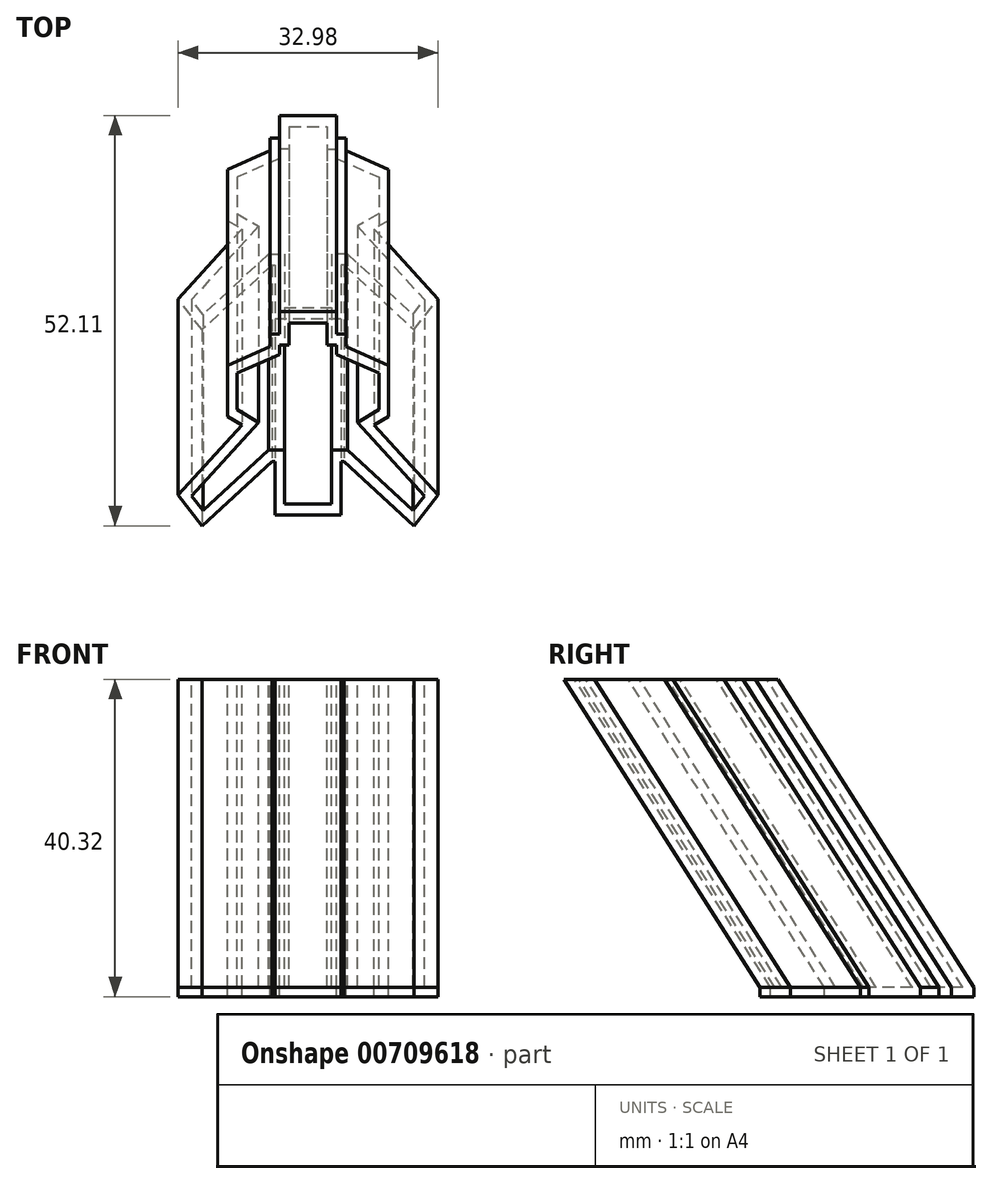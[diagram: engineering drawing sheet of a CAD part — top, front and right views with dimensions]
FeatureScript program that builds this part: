
annotation { "Feature Type Name" : "Feature", "Feature Type Description" : "" }
export const myFeature = defineFeature(function(context is Context, id is Id, definition is map)
    precondition{}
    {
        {
            var Q0;
            Q0=qCreatedBy(makeId("Top.planeOp"),FACE);
            var sketch = newSketch(context, id + "F0", { "sketchPlane" : qUnion([Q0])});
            skLineSegment(sketch, "E0", {"start": v(5, -3.24) * mm, "end": v(3, -3.24) * mm});
            skLineSegment(sketch, "E1", {"start": v(3, -3.24) * mm, "end": v(3, -9) * mm});
            skLineSegment(sketch, "E2", {"start": v(5, 0) * mm, "end": v(9, 2) * mm});
            skLineSegment(sketch, "E3", {"start": v(9, 5) * mm, "end": v(5, 7) * mm, "construction": true});
            skLineSegment(sketch, "E4", {"start": v(5, 7) * mm, "end": v(5, 9) * mm, "construction": true});
            skLineSegment(sketch, "E5", {"start": v(9, 5) * mm, "end": v(9, 2) * mm});
            skLineSegment(sketch, "E6.bottom", {"start": v(67.07, 3.45) * mm, "end": v(65.87, 3.45) * mm});
            skLineSegment(sketch, "E6.left", {"start": v(67.07, 3.45) * mm, "end": v(67.07, 4.65) * mm});
            skPoint(sketch, "E6.middle", {"position": v(53.07, 12.45) * mm});
            skLineSegment(sketch, "E7", {"start": v(67.07, 3.45) * mm, "end": v(67.07, 4.65) * mm, "construction": true});
            skLineSegment(sketch, "E8", {"start": v(58.07, 12.45) * mm, "end": v(67.07, 4.65) * mm});
            skLineSegment(sketch, "E9", {"start": v(67.07, 3.45) * mm, "end": v(65.87, 3.45) * mm, "construction": true});
            skLineSegment(sketch, "E10", {"start": v(65.87, 3.45) * mm, "end": v(58.07, 10.2) * mm});
            skLineSegment(sketch, "E11", {"start": v(58.07, 10.2) * mm, "end": v(58.07, 9.2) * mm});
            skLineSegment(sketch, "E12", {"start": v(58.07, 9.2) * mm, "end": v(56.07, 9.2) * mm});
            skLineSegment(sketch, "E13", {"start": v(56.07, 9.2) * mm, "end": v(56.07, 3.45) * mm});
            skLineSegment(sketch, "E14", {"start": v(56.07, 3.45) * mm, "end": v(53.07, 3.45) * mm});
            skLineSegment(sketch, "E15", {"start": v(58.07, 12.45) * mm, "end": v(62.07, 14.45) * mm});
            skLineSegment(sketch, "E16", {"start": v(62.07, 17.45) * mm, "end": v(58.07, 19.45) * mm});
            skLineSegment(sketch, "E17", {"start": v(58.07, 19.45) * mm, "end": v(58.07, 21.45) * mm});
            skLineSegment(sketch, "E18", {"start": v(62.07, 17.45) * mm, "end": v(62.07, 14.45) * mm});
            skLineSegment(sketch, "E19", {"start": v(58.07, 21.45) * mm, "end": v(53.07, 21.45) * mm});
            skLineSegment(sketch, "E20", {"start": v(3, -9) * mm, "end": v(0, -9) * mm});
            skLineSegment(sketch, "E21", {"start": v(5, 0) * mm, "end": v(6, 0) * mm});
            skLineSegment(sketch, "E22", {"start": v(0, 15.56) * mm, "end": v(0, -14.94) * mm, "construction": true});
            skPoint(sketch, "E23", {"position": v(14.8, -8.14) * mm});
            skPoint(sketch, "E24", {"position": v(13.33, -9.72) * mm});
            skLineSegment(sketch, "E25", {"start": v(5, -3.24) * mm, "end": v(13.33, -9.72) * mm});
            skLineSegment(sketch, "E26", {"start": v(6, 0) * mm, "end": v(14.8, -8.14) * mm});
            skLineSegment(sketch, "E27", {"start": v(13.33, -9.72) * mm, "end": v(14.8, -8.14) * mm});
            skLineSegment(sketch, "E28", {"start": v(0, 10.4) * mm, "end": v(2.4, 10.4) * mm});
            skLineSegment(sketch, "E29", {"start": v(2.4, 10.4) * mm, "end": v(2.4, 8) * mm});
            skLineSegment(sketch, "E30", {"start": v(2.4, 8) * mm, "end": v(3.6, 8) * mm});
            skLineSegment(sketch, "E31", {"start": v(3.6, 8) * mm, "end": v(3.6, 7) * mm});
            skLineSegment(sketch, "E32", {"start": v(3.6, 7) * mm, "end": v(9, 5) * mm});
            skLineSegment(sketch, "E33.MirrorCS", {"start": v(-13.33, -9.72) * mm, "end": v(-14.8, -8.14) * mm});
            skLineSegment(sketch, "E34.MirrorCS", {"start": v(-3.6, 8) * mm, "end": v(-3.6, 7) * mm});
            skLineSegment(sketch, "E35.MirrorCS", {"start": v(-2.4, 8) * mm, "end": v(-3.6, 8) * mm});
            skLineSegment(sketch, "E36.MirrorCS", {"start": v(-5, 0) * mm, "end": v(-6, 0) * mm});
            skLineSegment(sketch, "E37.MirrorCS", {"start": v(-5, -3.24) * mm, "end": v(-3, -3.24) * mm});
            skLineSegment(sketch, "E38.MirrorCS", {"start": v(-2.4, 10.4) * mm, "end": v(-2.4, 8) * mm});
            skLineSegment(sketch, "E39.MirrorCS", {"start": v(-3, -3.24) * mm, "end": v(-3, -9) * mm});
            skLineSegment(sketch, "E40.MirrorCS", {"start": v(-6, 0) * mm, "end": v(-14.8, -8.14) * mm});
            skLineSegment(sketch, "E41.MirrorCS", {"start": v(-3, -9) * mm, "end": v(0, -9) * mm});
            skLineSegment(sketch, "E42.MirrorCS", {"start": v(-3.6, 7) * mm, "end": v(-9, 5) * mm});
            skLineSegment(sketch, "E43.MirrorCS", {"start": v(-5, -3.24) * mm, "end": v(-13.33, -9.72) * mm});
            skLineSegment(sketch, "E44.MirrorCS", {"start": v(-9, 5) * mm, "end": v(-9, 2) * mm});
            skLineSegment(sketch, "E45.MirrorCS", {"start": v(-5, 0) * mm, "end": v(-9, 2) * mm});
            skLineSegment(sketch, "E46.MirrorCS", {"start": v(0, 10.4) * mm, "end": v(-2.4, 10.4) * mm});
            skPoint(sketch, "E47.MirrorP", {"position": v(-14.8, -8.14) * mm});
            skPoint(sketch, "E48.MirrorP", {"position": v(-13.33, -9.72) * mm});
            skLineSegment(sketch, "E49.0", {"start": v(-7.74, 0.03) * mm, "end": v(-16.5, -8.07) * mm});
            skLineSegment(sketch, "E49.1", {"start": v(-13.46, -11.35) * mm, "end": v(-16.5, -8.07) * mm});
            skLineSegment(sketch, "E49.2", {"start": v(-4.59, -4.44) * mm, "end": v(-13.46, -11.35) * mm});
            skLineSegment(sketch, "E49.3", {"start": v(4.8, 9.2) * mm, "end": v(4.8, 7.84) * mm});
            skLineSegment(sketch, "E49.4", {"start": v(3.6, 9.2) * mm, "end": v(4.8, 9.2) * mm});
            skLineSegment(sketch, "E49.5", {"start": v(3.6, 11.6) * mm, "end": v(3.6, 9.2) * mm});
            skLineSegment(sketch, "E49.6", {"start": v(0, 11.6) * mm, "end": v(3.6, 11.6) * mm});
            skLineSegment(sketch, "E49.7", {"start": v(0, 11.6) * mm, "end": v(-3.6, 11.6) * mm});
            skLineSegment(sketch, "E49.8", {"start": v(-3.6, 11.6) * mm, "end": v(-3.6, 9.2) * mm});
            skLineSegment(sketch, "E49.9", {"start": v(-10.2, 5.84) * mm, "end": v(-10.2, 1.26) * mm});
            skLineSegment(sketch, "E49.10", {"start": v(-4.8, 7.84) * mm, "end": v(-10.2, 5.84) * mm});
            skLineSegment(sketch, "E49.11", {"start": v(-4.8, 9.2) * mm, "end": v(-4.8, 7.84) * mm});
            skLineSegment(sketch, "E49.12", {"start": v(-3.6, 9.2) * mm, "end": v(-4.8, 9.2) * mm});
            skLineSegment(sketch, "E49.13", {"start": v(4.8, 7.84) * mm, "end": v(10.2, 5.84) * mm});
            skLineSegment(sketch, "E49.14", {"start": v(10.2, 5.84) * mm, "end": v(10.2, 1.26) * mm});
            skLineSegment(sketch, "E49.15", {"start": v(7.74, 0.03) * mm, "end": v(10.2, 1.26) * mm});
            skLineSegment(sketch, "E49.16", {"start": v(-7.74, 0.03) * mm, "end": v(-10.2, 1.26) * mm});
            skLineSegment(sketch, "E49.17", {"start": v(7.74, 0.03) * mm, "end": v(16.5, -8.07) * mm});
            skLineSegment(sketch, "E49.18", {"start": v(13.46, -11.35) * mm, "end": v(16.5, -8.07) * mm});
            skLineSegment(sketch, "E49.19", {"start": v(4.59, -4.44) * mm, "end": v(13.46, -11.35) * mm});
            skLineSegment(sketch, "E49.20", {"start": v(4.59, -4.44) * mm, "end": v(4.2, -4.44) * mm});
            skLineSegment(sketch, "E49.21", {"start": v(4.2, -4.44) * mm, "end": v(4.2, -10.2) * mm});
            skLineSegment(sketch, "E49.22", {"start": v(4.2, -10.2) * mm, "end": v(0, -10.2) * mm});
            skLineSegment(sketch, "E49.23", {"start": v(-4.2, -10.2) * mm, "end": v(0, -10.2) * mm});
            skLineSegment(sketch, "E49.24", {"start": v(-4.2, -4.44) * mm, "end": v(-4.2, -10.2) * mm});
            skLineSegment(sketch, "E49.25", {"start": v(-4.59, -4.44) * mm, "end": v(-4.2, -4.44) * mm});
            skSolve(sketch);
        }
        {
            var Q0;
            Q0=makeQuery(id+"F0.imprint","IMPRINT",FACE,{"disambiguationData":[TD([[makeQuery(id+"F0.imprint","IMPRINT",EDGE,{"derivedFrom":sQuery(id+"F0.wireOp",EDGE,"E0")}),1.0]])]});
            extrude(context, id + "F1", {"entities" : qUnion([Q0]), "depth" : 3 * mm, "offsetDistance" : 25 * mm});
        }
        {
            var Q0;
            Q0=qCreatedBy(makeId("Top.planeOp"),FACE);
            var sketch = newSketch(context, id + "F2", { "sketchPlane" : qUnion([Q0])});
            skLineSegment(sketch, "E50", {"start": v(-27.03, 0) * mm, "end": v(31.48, 0) * mm});
            skSolve(sketch);
        }
        {
            var Q0;
            Q0=sQuery(id+"F2.wireOp",EDGE,"E50");
            cPlane(context, id + "F3", {"entities" : qUnion([Q0]), "cplaneType" : CPlaneType.LINE_ANGLE, "offset" : 25 * mm, "angle" : 57.5 * degree, "oppositeDirection" : true, "width" : 150 * mm, "height" : 150 * mm});
        }
        {
            var Q0;
            Q0=qCreatedBy(id+"F3.planeOp",FACE);
            var sketch = newSketch(context, id + "F4", { "sketchPlane" : qUnion([Q0])});
            skLineSegment(sketch, "E51", {"start": v(-5, 3.55) * mm, "end": v(-3, 3.55) * mm});
            skLineSegment(sketch, "E52", {"start": v(-3, 3.55) * mm, "end": v(-3, 9.31) * mm});
            skLineSegment(sketch, "E53", {"start": v(-9, -4.69) * mm, "end": v(-5, -6.69) * mm, "construction": true});
            skLineSegment(sketch, "E54", {"start": v(-5, -6.69) * mm, "end": v(-5, -8.69) * mm, "construction": true});
            skLineSegment(sketch, "E55", {"start": v(-3, 9.31) * mm, "end": v(0, 9.31) * mm});
            skLineSegment(sketch, "E56", {"start": v(0, -15.25) * mm, "end": v(0, 15.25) * mm, "construction": true});
            skPoint(sketch, "E57", {"position": v(-14.8, 8.45) * mm});
            skPoint(sketch, "E58", {"position": v(-13.33, 10.03) * mm});
            skLineSegment(sketch, "E59", {"start": v(-5, 3.55) * mm, "end": v(-13.33, 10.03) * mm});
            skLineSegment(sketch, "E60", {"start": v(-13.33, 10.03) * mm, "end": v(-14.8, 8.45) * mm});
            skLineSegment(sketch, "E61", {"start": v(0, -10.09) * mm, "end": v(-2.4, -10.09) * mm});
            skLineSegment(sketch, "E62", {"start": v(-2.4, -10.09) * mm, "end": v(-2.4, -7.69) * mm});
            skLineSegment(sketch, "E63", {"start": v(-2.4, -7.69) * mm, "end": v(-3.6, -7.69) * mm});
            skLineSegment(sketch, "E64", {"start": v(-3.6, -7.69) * mm, "end": v(-3.6, -6.69) * mm});
            skLineSegment(sketch, "E65", {"start": v(-3.6, -6.69) * mm, "end": v(-9, -4.69) * mm});
            skLineSegment(sketch, "E66.MirrorCS", {"start": v(13.33, 10.03) * mm, "end": v(14.8, 8.45) * mm});
            skLineSegment(sketch, "E67.MirrorCS", {"start": v(3.6, -7.69) * mm, "end": v(3.6, -6.69) * mm});
            skLineSegment(sketch, "E68.MirrorCS", {"start": v(2.4, -7.69) * mm, "end": v(3.6, -7.69) * mm});
            skLineSegment(sketch, "E69.MirrorCS", {"start": v(5, 3.55) * mm, "end": v(3, 3.55) * mm});
            skLineSegment(sketch, "E70.MirrorCS", {"start": v(2.4, -10.09) * mm, "end": v(2.4, -7.69) * mm});
            skLineSegment(sketch, "E71.MirrorCS", {"start": v(3, 3.55) * mm, "end": v(3, 9.31) * mm});
            skLineSegment(sketch, "E72.MirrorCS", {"start": v(6.28, 0.57) * mm, "end": v(14.8, 8.45) * mm});
            skLineSegment(sketch, "E73.MirrorCS", {"start": v(3, 9.31) * mm, "end": v(0, 9.31) * mm});
            skLineSegment(sketch, "E74.MirrorCS", {"start": v(3.6, -6.69) * mm, "end": v(9, -4.69) * mm});
            skLineSegment(sketch, "E75.MirrorCS", {"start": v(5, 3.55) * mm, "end": v(13.33, 10.03) * mm});
            skLineSegment(sketch, "E76.MirrorCS", {"start": v(0, -10.09) * mm, "end": v(2.4, -10.09) * mm});
            skPoint(sketch, "E77.MirrorP", {"position": v(14.8, 8.45) * mm});
            skPoint(sketch, "E78.MirrorP", {"position": v(13.33, 10.03) * mm});
            skLineSegment(sketch, "E79.1", {"start": v(13.46, 11.66) * mm, "end": v(16.5, 8.38) * mm});
            skLineSegment(sketch, "E79.2", {"start": v(4.59, 4.75) * mm, "end": v(13.46, 11.66) * mm});
            skLineSegment(sketch, "E79.3", {"start": v(-4.8, -8.89) * mm, "end": v(-4.8, -7.52) * mm});
            skLineSegment(sketch, "E79.4", {"start": v(-3.6, -8.89) * mm, "end": v(-4.8, -8.89) * mm});
            skLineSegment(sketch, "E79.5", {"start": v(-3.6, -11.29) * mm, "end": v(-3.6, -8.89) * mm});
            skLineSegment(sketch, "E79.6", {"start": v(0, -11.29) * mm, "end": v(-3.6, -11.29) * mm});
            skLineSegment(sketch, "E79.7", {"start": v(0, -11.29) * mm, "end": v(3.6, -11.29) * mm});
            skLineSegment(sketch, "E79.8", {"start": v(3.6, -11.29) * mm, "end": v(3.6, -8.89) * mm});
            skLineSegment(sketch, "E79.10", {"start": v(4.8, -7.52) * mm, "end": v(10.2, -5.52) * mm});
            skLineSegment(sketch, "E79.11", {"start": v(4.8, -8.89) * mm, "end": v(4.8, -7.52) * mm});
            skLineSegment(sketch, "E79.12", {"start": v(3.6, -8.89) * mm, "end": v(4.8, -8.89) * mm});
            skLineSegment(sketch, "E79.13", {"start": v(-4.8, -7.52) * mm, "end": v(-10.2, -5.52) * mm});
            skLineSegment(sketch, "E79.18", {"start": v(-13.46, 11.66) * mm, "end": v(-16.5, 8.38) * mm});
            skLineSegment(sketch, "E79.19", {"start": v(-4.59, 4.75) * mm, "end": v(-13.46, 11.66) * mm});
            skLineSegment(sketch, "E79.20", {"start": v(-4.59, 4.75) * mm, "end": v(-4.2, 4.75) * mm});
            skLineSegment(sketch, "E79.21", {"start": v(-4.2, 4.75) * mm, "end": v(-4.2, 10.51) * mm});
            skLineSegment(sketch, "E79.22", {"start": v(-4.2, 10.51) * mm, "end": v(0, 10.51) * mm});
            skLineSegment(sketch, "E79.23", {"start": v(4.2, 10.51) * mm, "end": v(0, 10.51) * mm});
            skLineSegment(sketch, "E79.24", {"start": v(4.2, 4.75) * mm, "end": v(4.2, 10.51) * mm});
            skLineSegment(sketch, "E79.25", {"start": v(4.59, 4.75) * mm, "end": v(4.2, 4.75) * mm});
            skLineSegment(sketch, "E80", {"start": v(9, -4.69) * mm, "end": v(9, -0.8) * mm});
            skLineSegment(sketch, "E81", {"start": v(9, -0.8) * mm, "end": v(6.28, 0.57) * mm});
            skLineSegment(sketch, "E82.0", {"start": v(8.37, 0.86) * mm, "end": v(16.5, 8.38) * mm});
            skLineSegment(sketch, "E82.1", {"start": v(10.2, -0.05) * mm, "end": v(8.37, 0.86) * mm});
            skLineSegment(sketch, "E82.2", {"start": v(10.2, -5.52) * mm, "end": v(10.2, -0.05) * mm});
            skLineSegment(sketch, "E83.MirrorCS", {"start": v(-6.28, 0.57) * mm, "end": v(-14.8, 8.45) * mm});
            skLineSegment(sketch, "E84.MirrorCS", {"start": v(-8.37, 0.86) * mm, "end": v(-16.5, 8.38) * mm});
            skLineSegment(sketch, "E85.MirrorCS", {"start": v(-10.2, -0.05) * mm, "end": v(-8.37, 0.86) * mm});
            skLineSegment(sketch, "E86.MirrorCS", {"start": v(-9, -0.8) * mm, "end": v(-6.28, 0.57) * mm});
            skLineSegment(sketch, "E87.MirrorCS", {"start": v(-9, -4.69) * mm, "end": v(-9, -0.8) * mm});
            skLineSegment(sketch, "E88.MirrorCS", {"start": v(-10.2, -5.52) * mm, "end": v(-10.2, -0.05) * mm});
            skSolve(sketch);
        }
        {
            var Q0;
            Q0=qCreatedBy(makeId("Front.planeOp"),FACE);
            var sketch = newSketch(context, id + "F5", { "sketchPlane" : qUnion([Q0])});
            skPoint(sketch, "E89.0", {"position": v(-27.03, 0) * mm});
            skLineSegment(sketch, "E90", {"start": v(0, 0) * mm, "end": v(0, -39.12) * mm});
            skLineSegment(sketch, "E91", {"start": v(-53.83, -39.12) * mm, "end": v(63, -39.12) * mm});
            skLineSegment(sketch, "E92", {"start": v(63, -39.12) * mm, "end": v(63, -40.32) * mm});
            skLineSegment(sketch, "E93", {"start": v(63, -40.32) * mm, "end": v(-53.83, -40.32) * mm});
            skLineSegment(sketch, "E94", {"start": v(-53.83, -40.32) * mm, "end": v(-53.83, -39.12) * mm});
            skSolve(sketch);
        }
        {
            var Q0;
            {var subQ0=sQuery(id+"F5.wireOp",EDGE,"E92");Q0=makeQuery(id+"F5.imprint","IMPRINT",FACE,{"disambiguationData":[TD([[makeQuery(id+"F5.imprint","IMPRINT",EDGE,{"derivedFrom":subQ0}),-1.0]])]});}
            extrude(context, id + "F6", {"entities" : qUnion([Q0]), "oppositeDirection" : true, "depth" : 125 * mm, "offsetDistance" : 25 * mm, "symmetric" : true});
        }
        {
            var Q0;
            Q0=qCreatedBy(makeId("Right.planeOp"),FACE);
            var sketch = newSketch(context, id + "F7", { "sketchPlane" : qUnion([Q0])});
            skLineSegment(sketch, "E95", {"start": v(-25, 0) * mm, "end": v(75, 0) * mm});
            skLineSegment(sketch, "E96", {"start": v(75, 0) * mm, "end": v(75, 20) * mm});
            skLineSegment(sketch, "E97", {"start": v(75, 20) * mm, "end": v(-25, 20) * mm});
            skLineSegment(sketch, "E98", {"start": v(-25, 20) * mm, "end": v(-25, 0) * mm});
            skSolve(sketch);
        }
        {
            var Q0;
            Q0 = qSketchRegion(id + "F4", true);
            var Q1;
            Q1=makeQuery(id+"F6.opExtrude","SWEPT_FACE",FACE,{"disambiguationData":[OSD([sQuery(id+"F5.wireOp",EDGE,"E91")])]});
            extrude(context, id + "F8", {"entities" : qUnion([Q0]), "endBound" : BoundingType.UP_TO_SURFACE, "depth" : 25 * mm, "endBoundEntityFace" : qUnion([Q1]), "offsetDistance" : 25 * mm, "hasSecondDirection" : true, "secondDirectionOppositeDirection" : true, "secondDirectionDepth" : 15 * mm});
        }
        {
            var Q0;
            Q0=makeQuery(id+"F7.imprint","IMPRINT",FACE,{"disambiguationData":[TD([[makeQuery(id+"F7.imprint","IMPRINT",EDGE,{"derivedFrom":sQuery(id+"F7.wireOp",EDGE,"E95")}),1.0]])]});
            extrude(context, id + "F9", {"entities" : qUnion([Q0]), "operationType" : NewBodyOperationType.REMOVE, "oppositeDirection" : true, "depth" : 200 * mm, "offsetDistance" : 25 * mm, "symmetric" : true});
        }
        {
            var Q0;
            Q0=makeQuery(id+"F6.opExtrude","SWEPT_FACE",FACE,{"disambiguationData":[OSD([sQuery(id+"F5.wireOp",EDGE,"E91")])]});
            var sketch = newSketch(context, id + "F10", { "sketchPlane" : qUnion([Q0])});
            skLineSegment(sketch, "E99.bottom", {"start": v(69.39, 69.74) * mm, "end": v(-69.39, 69.74) * mm});
            skLineSegment(sketch, "E99.top", {"start": v(69.39, -69.74) * mm, "end": v(-69.39, -69.74) * mm});
            skLineSegment(sketch, "E99.left", {"start": v(69.39, 69.74) * mm, "end": v(69.39, -69.74) * mm});
            skLineSegment(sketch, "E99.right", {"start": v(-69.39, 69.74) * mm, "end": v(-69.39, -69.74) * mm});
            skPoint(sketch, "E99.middle", {"position": v(0, 0) * mm});
            skSolve(sketch);
        }
        {
            var Q0;
            Q0=makeQuery(id+"F10.imprint","IMPRINT",FACE,{"disambiguationData":[TD([[makeQuery(id+"F10.imprint","IMPRINT",EDGE,{"derivedFrom":sQuery(id+"F10.wireOp",EDGE,"E99.bottom")}),1.0]])]});
            var Q1;
            Q1=makeQuery(id+"F6.opExtrude","SWEPT_FACE",FACE,{"disambiguationData":[OSD([sQuery(id+"F5.wireOp",EDGE,"E93")])]});
            var Q2;
            {var subQ0=sQuery(id+"F5.wireOp",EDGE,"E91");Q2=makeQuery(id+"F10.imprint","IMPRINT",FACE,{"disambiguationData":[TD([[makeQuery(id+"F10.imprint","IMPRINT",EDGE,{"derivedFrom":makeQuery(id+"F6.opExtrude","CAP_EDGE",EDGE,{"disambiguationData":[OSD([subQ0])],"isStart":true})}),1.0]])]});}
            extrude(context, id + "F11", {"entities" : qUnion([Q0, Q1, Q2]), "operationType" : NewBodyOperationType.REMOVE, "oppositeDirection" : true, "depth" : 25 * mm, "offsetDistance" : 25 * mm});
        }
        {
            var Q0;
            Q0=makeQuery(id+"F8.opExtrude","CAP_FACE",FACE,{"disambiguationData":[OSD([sQuery(id+"F4.wireOp",EDGE,"E51"),sQuery(id+"F4.wireOp",EDGE,"E52"),sQuery(id+"F4.wireOp",EDGE,"d26377e8-06a3-4805-bd2a-4534d5efe636"),sQuery(id+"F4.wireOp",EDGE,"7f882d78-4364-4cfe-9342-b45333ac8082"),sQuery(id+"F4.wireOp",EDGE,"E55"),sQuery(id+"F4.wireOp",EDGE,"64a004a5-97f6-4a91-8b34-b787f2fb5424"),sQuery(id+"F4.wireOp",EDGE,"E59"),sQuery(id+"F4.wireOp",EDGE,"997694c6-7273-4e5d-ab2a-2809bc0465a4"),sQuery(id+"F4.wireOp",EDGE,"E60"),sQuery(id+"F4.wireOp",EDGE,"E61"),sQuery(id+"F4.wireOp",EDGE,"E62"),sQuery(id+"F4.wireOp",EDGE,"E63"),sQuery(id+"F4.wireOp",EDGE,"E64"),sQuery(id+"F4.wireOp",EDGE,"E65"),sQuery(id+"F4.wireOp",EDGE,"E66.MirrorCS"),sQuery(id+"F4.wireOp",EDGE,"E67.MirrorCS"),sQuery(id+"F4.wireOp",EDGE,"E68.MirrorCS"),sQuery(id+"F4.wireOp",EDGE,"3529dfb3-b490-43c7-97e3-393a9e17953b.MirrorCS"),sQuery(id+"F4.wireOp",EDGE,"E69.MirrorCS"),sQuery(id+"F4.wireOp",EDGE,"E70.MirrorCS"),sQuery(id+"F4.wireOp",EDGE,"E71.MirrorCS"),sQuery(id+"F4.wireOp",EDGE,"E72.MirrorCS"),sQuery(id+"F4.wireOp",EDGE,"E73.MirrorCS"),sQuery(id+"F4.wireOp",EDGE,"E74.MirrorCS"),sQuery(id+"F4.wireOp",EDGE,"E75.MirrorCS"),sQuery(id+"F4.wireOp",EDGE,"f3844805-b8bc-47cf-b3eb-640eb4894aef.MirrorCS"),sQuery(id+"F4.wireOp",EDGE,"8f11244f-9f45-4f7e-8854-c22a0b217610.MirrorCS"),sQuery(id+"F4.wireOp",EDGE,"E76.MirrorCS"),sQuery(id+"F4.wireOp",EDGE,"E79.0"),sQuery(id+"F4.wireOp",EDGE,"E79.1"),sQuery(id+"F4.wireOp",EDGE,"E79.2"),sQuery(id+"F4.wireOp",EDGE,"E79.3"),sQuery(id+"F4.wireOp",EDGE,"E79.4"),sQuery(id+"F4.wireOp",EDGE,"E79.5"),sQuery(id+"F4.wireOp",EDGE,"E79.6"),sQuery(id+"F4.wireOp",EDGE,"E79.7"),sQuery(id+"F4.wireOp",EDGE,"E79.8"),sQuery(id+"F4.wireOp",EDGE,"E79.9"),sQuery(id+"F4.wireOp",EDGE,"E79.10"),sQuery(id+"F4.wireOp",EDGE,"E79.11"),sQuery(id+"F4.wireOp",EDGE,"E79.12"),sQuery(id+"F4.wireOp",EDGE,"E79.13"),sQuery(id+"F4.wireOp",EDGE,"E79.14"),sQuery(id+"F4.wireOp",EDGE,"E79.15"),sQuery(id+"F4.wireOp",EDGE,"E79.16"),sQuery(id+"F4.wireOp",EDGE,"E79.17"),sQuery(id+"F4.wireOp",EDGE,"E79.18"),sQuery(id+"F4.wireOp",EDGE,"E79.19"),sQuery(id+"F4.wireOp",EDGE,"E79.20"),sQuery(id+"F4.wireOp",EDGE,"E79.21"),sQuery(id+"F4.wireOp",EDGE,"E79.22"),sQuery(id+"F4.wireOp",EDGE,"E79.23"),sQuery(id+"F4.wireOp",EDGE,"E79.24"),sQuery(id+"F4.wireOp",EDGE,"E79.25")])],"isStart":false});
            var sketch = newSketch(context, id + "F12", { "sketchPlane" : qUnion([Q0])});
            skLineSegment(sketch, "E100.0", {"start": v(3.6, -38.3) * mm, "end": v(-3.6, -38.3) * mm});
            skLineSegment(sketch, "E100.1", {"start": v(-3.6, -38.3) * mm, "end": v(-3.6, -35.45) * mm});
            skLineSegment(sketch, "E100.2", {"start": v(-4.8, -35.45) * mm, "end": v(-4.8, -33.83) * mm});
            skLineSegment(sketch, "E100.3", {"start": v(-3.6, -35.45) * mm, "end": v(-4.8, -35.45) * mm});
            skLineSegment(sketch, "E100.4", {"start": v(-4.8, -33.83) * mm, "end": v(-10.2, -31.46) * mm});
            skLineSegment(sketch, "E100.5", {"start": v(-10.2, -31.46) * mm, "end": v(-10.2, -24.97) * mm});
            skLineSegment(sketch, "E100.6", {"start": v(4.8, -33.83) * mm, "end": v(10.2, -31.46) * mm});
            skLineSegment(sketch, "E100.7", {"start": v(4.8, -35.45) * mm, "end": v(4.8, -33.83) * mm});
            skLineSegment(sketch, "E100.8", {"start": v(3.6, -35.45) * mm, "end": v(4.8, -35.45) * mm});
            skLineSegment(sketch, "E100.9", {"start": v(3.6, -38.3) * mm, "end": v(3.6, -35.45) * mm});
            skLineSegment(sketch, "E100.10", {"start": v(10.2, -31.46) * mm, "end": v(10.2, -24.97) * mm});
            skLineSegment(sketch, "E100.11", {"start": v(10.2, -24.97) * mm, "end": v(8.37, -23.89) * mm});
            skLineSegment(sketch, "E100.12", {"start": v(8.37, -23.89) * mm, "end": v(16.5, -14.97) * mm});
            skLineSegment(sketch, "E100.13", {"start": v(-8.37, -23.89) * mm, "end": v(-16.5, -14.97) * mm});
            skLineSegment(sketch, "E100.14", {"start": v(-10.2, -24.97) * mm, "end": v(-8.37, -23.89) * mm});
            skLineSegment(sketch, "E101.0", {"start": v(13.46, -11.09) * mm, "end": v(16.5, -14.97) * mm});
            skLineSegment(sketch, "E101.1", {"start": v(4.59, -19.28) * mm, "end": v(13.46, -11.09) * mm});
            skLineSegment(sketch, "E101.2", {"start": v(4.2, -19.28) * mm, "end": v(4.2, -12.45) * mm});
            skLineSegment(sketch, "E101.3", {"start": v(-4.2, -19.28) * mm, "end": v(-4.2, -12.45) * mm});
            skLineSegment(sketch, "E101.4", {"start": v(4.2, -12.45) * mm, "end": v(-4.2, -12.45) * mm});
            skLineSegment(sketch, "E101.5", {"start": v(-4.59, -19.28) * mm, "end": v(-13.46, -11.09) * mm});
            skLineSegment(sketch, "E101.6", {"start": v(-13.46, -11.09) * mm, "end": v(-16.5, -14.97) * mm});
            skLineSegment(sketch, "E102.0", {"start": v(-4.59, -19.28) * mm, "end": v(-4.2, -19.28) * mm});
            skLineSegment(sketch, "E102.1", {"start": v(4.59, -19.28) * mm, "end": v(4.2, -19.28) * mm});
            skSolve(sketch);
        }
        {
            var Q0;
            Q0=makeQuery(id+"F12.imprint","IMPRINT",FACE,{"disambiguationData":[TD([[makeQuery(id+"F12.imprint","IMPRINT",EDGE,{"derivedFrom":sQuery(id+"F12.wireOp",EDGE,"E100.0")}),-1.0]])]});
            var Q1;
            Q1=makeQuery(id+"F12.imprint","IMPRINT",FACE,{"disambiguationData":[TD([[makeQuery(id+"F12.imprint","IMPRINT",EDGE,{"derivedFrom":makeQuery(id+"F8.opExtrude","CAP_EDGE",EDGE,{"disambiguationData":[OSD([sQuery(id+"F4.wireOp",EDGE,"E51")])],"isStart":false})}),-1.0]])]});
            extrude(context, id + "F13", {"entities" : qUnion([Q0, Q1]), "operationType" : NewBodyOperationType.ADD, "depth" : 1.2 * mm, "offsetDistance" : 25 * mm});
        }
    });
